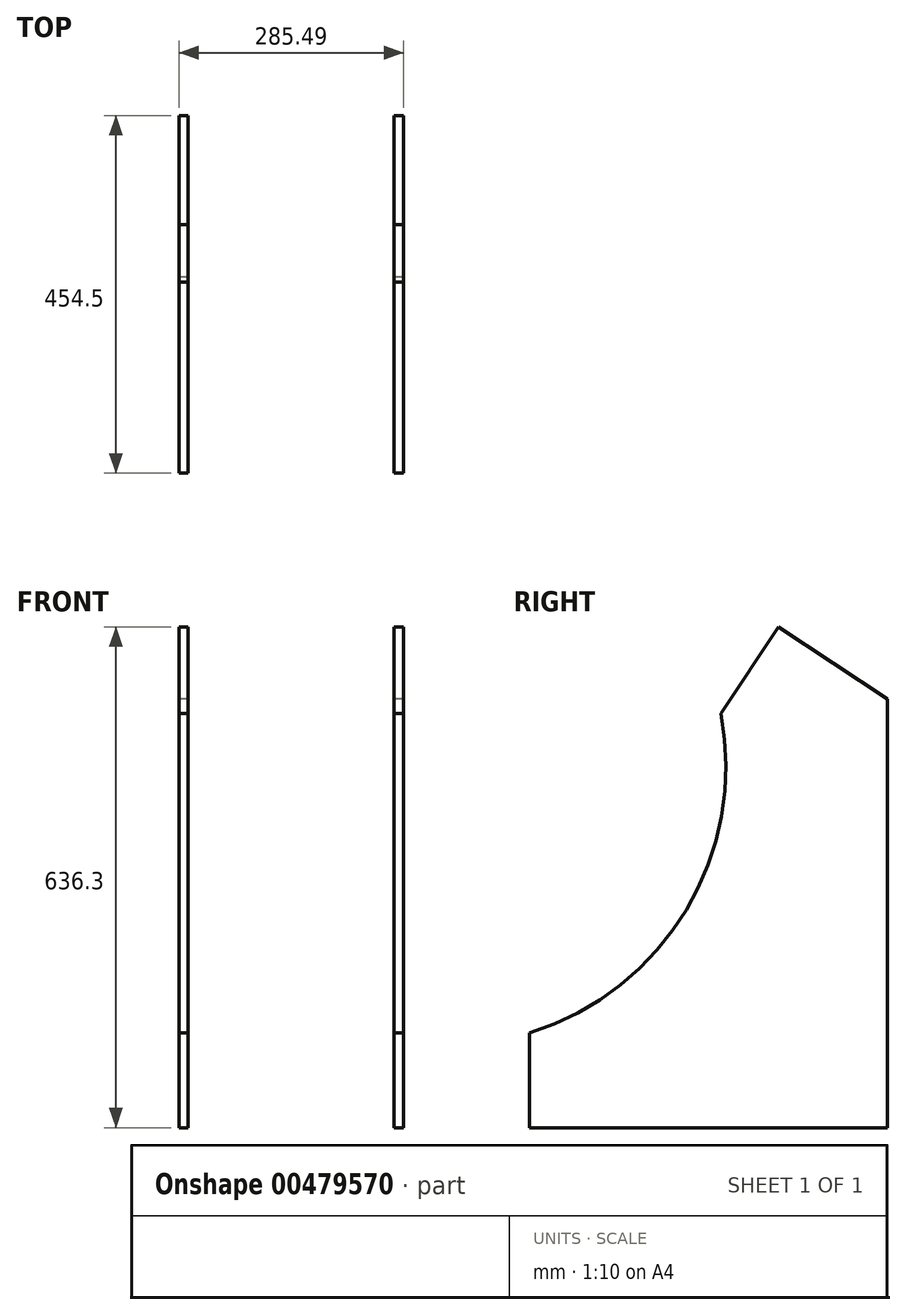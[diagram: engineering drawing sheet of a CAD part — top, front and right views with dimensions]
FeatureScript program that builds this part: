
annotation { "Feature Type Name" : "Feature", "Feature Type Description" : "" }
export const myFeature = defineFeature(function(context is Context, id is Id, definition is map)
    precondition{}
    {
        {
            var Q0;
            Q0=qCreatedBy(makeId("Right.planeOp"),FACE);
            var sketch = newSketch(context, id + "F0", { "sketchPlane" : qUnion([Q0])});
            skLineSegment(sketch, "E0.bottom", {"start": v(0, 0) * mm, "end": v(-454.5, 0) * mm});
            skLineSegment(sketch, "E0.top", {"start": v(0, 636.3) * mm, "end": v(-454.5, 636.3) * mm});
            skLineSegment(sketch, "E0.left", {"start": v(0, 0) * mm, "end": v(0, 636.3) * mm});
            skLineSegment(sketch, "E0.right", {"start": v(-454.5, 0) * mm, "end": v(-454.5, 636.3) * mm});
            skLineSegment(sketch, "E1", {"start": v(-454.5, 0) * mm, "end": v(-454.5, 120.4) * mm});
            skLineSegment(sketch, "E2", {"start": v(0, 0) * mm, "end": v(0, 544.3) * mm});
            skLineSegment(sketch, "E3", {"start": v(0, 544.3) * mm, "end": v(-138.65, 636.3) * mm});
            skLineSegment(sketch, "E4", {"start": v(-138.65, 636.3) * mm, "end": v(-211.63, 526.3) * mm});
            skArc(sketch, "E5", {"start": v(-454.5, 120.4) * mm, "mid": v(-255.4, 276.88) * mm, "end": v(-211.63, 526.3) * mm});
            skSolve(sketch);
        }
        {
            var Q0;
            Q0=makeQuery(id+"F0.imprint","IMPRINT",FACE,{"disambiguationData":[TD([[makeQuery(id+"F0.imprint","IMPRINT",EDGE,{"derivedFrom":sQuery(id+"F0.wireOp",EDGE,"E0.bottom")}),-1.0]])]});
            extrude(context, id + "F1", {"entities" : qUnion([Q0]), "depth" : 12 * mm});
        }
        {
            var Q0;
            Q0=makeQuery(id+"F1.opExtrude","SWEPT_BODY",BODY,{"disambiguationData":[OSD([sQuery(id+"F0.wireOp",EDGE,"E0.bottom"),sQuery(id+"F0.wireOp",EDGE,"E1"),sQuery(id+"F0.wireOp",EDGE,"E2"),sQuery(id+"F0.wireOp",EDGE,"E3"),sQuery(id+"F0.wireOp",EDGE,"E4"),sQuery(id+"F0.wireOp",EDGE,"E5")])]});
            transform(context, id + "F2", {"entities" : qUnion([Q0]), "transformType" : TransformType.TRANSLATION_3D, "dx" : 500 * mm, "dy" : 0 * mm, "dz" : 0 * mm, "makeCopy" : true});
        }
        {
            var Q0;
            Q0=makeQuery(id+"F2.opPattern","COPY",BODY,{"derivedFrom":makeQuery(id+"F1.opExtrude","SWEPT_BODY",BODY,{"disambiguationData":[OSD([sQuery(id+"F0.wireOp",EDGE,"E0.bottom"),sQuery(id+"F0.wireOp",EDGE,"E1"),sQuery(id+"F0.wireOp",EDGE,"E2"),sQuery(id+"F0.wireOp",EDGE,"E3"),sQuery(id+"F0.wireOp",EDGE,"E4"),sQuery(id+"F0.wireOp",EDGE,"E5")])]}),"instanceName":"1"});
            transform(context, id + "F3", {"entities" : qUnion([Q0]), "transformType" : TransformType.TRANSLATION_3D, "dx" : -773.5 * mm, "dy" : 0 * mm, "dz" : 0 * mm, "makeCopy" : false});
        }
        {
            var Q0;
            Q0=makeQuery(id+"F1.opExtrude","SWEPT_FACE",FACE,{"disambiguationData":[OSD([sQuery(id+"F0.wireOp",EDGE,"E0.bottom")])]});
            cPlane(context, id + "F4", {"entities" : qUnion([Q0]), "cplaneType" : CPlaneType.OFFSET, "offset" : 0 * mm, "width" : 150 * mm, "height" : 150 * mm});
        }
    });
